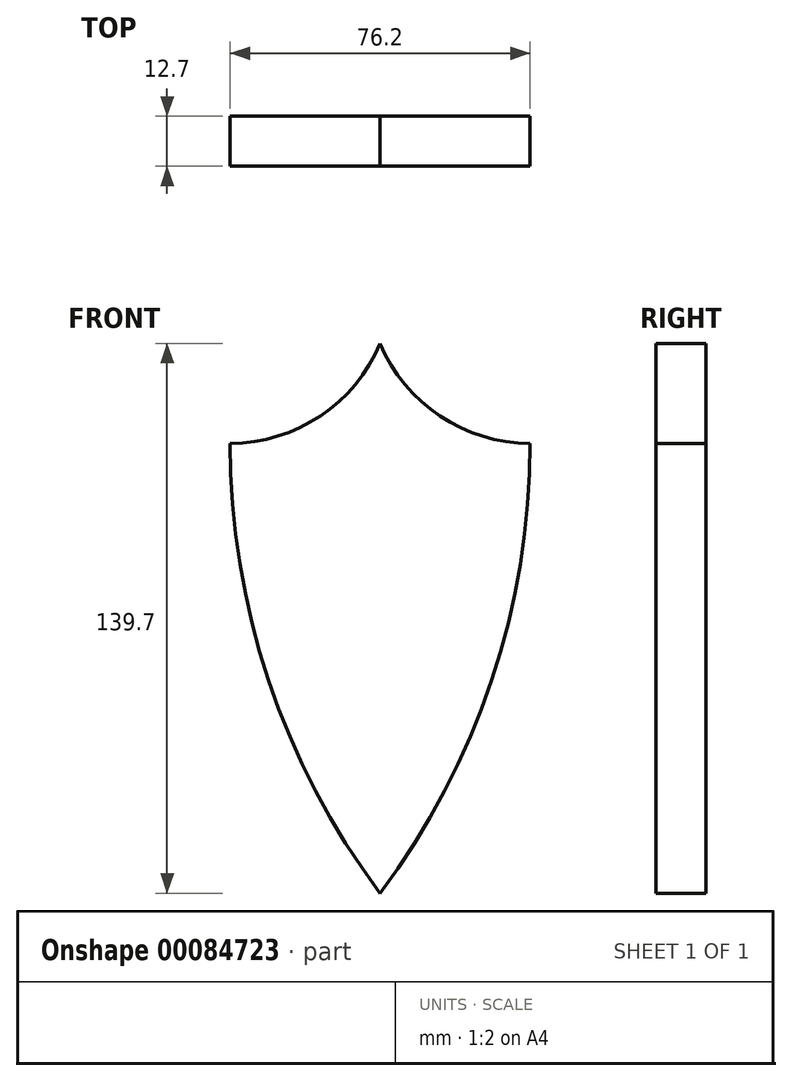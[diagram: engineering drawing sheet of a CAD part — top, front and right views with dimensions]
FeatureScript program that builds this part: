
annotation { "Feature Type Name" : "Feature", "Feature Type Description" : "" }
export const myFeature = defineFeature(function(context is Context, id is Id, definition is map)
    precondition{}
    {
        {
            var Q0;
            Q0=qCreatedBy(makeId("Front.planeOp"),FACE);
            var sketch = newSketch(context, id + "F0", { "sketchPlane" : qUnion([Q0])});
            skLineSegment(sketch, "E0", {"start": v(0, -38.1) * mm, "end": v(0, 0) * mm});
            skLineSegment(sketch, "E1", {"start": v(0, 0) * mm, "end": v(-38.1, 0) * mm});
            skLineSegment(sketch, "E2", {"start": v(0, 0) * mm, "end": v(0, 25.4) * mm});
            skLineSegment(sketch, "E3", {"start": v(0, -38.1) * mm, "end": v(0, -114.3) * mm});
            skArc(sketch, "E4", {"start": v(-38.1, 0) * mm, "mid": v(-28.32, -60.24) * mm, "end": v(0, -114.3) * mm});
            skArc(sketch, "E5", {"start": v(-38.1, 0) * mm, "mid": v(-15.2, 6.93) * mm, "end": v(0, 25.4) * mm});
            skArc(sketch, "E6.MirrorCS", {"start": v(38.1, 0) * mm, "mid": v(28.32, -60.24) * mm, "end": v(0, -114.3) * mm});
            skLineSegment(sketch, "E7.MirrorCS", {"start": v(0, 0) * mm, "end": v(38.1, 0) * mm});
            skArc(sketch, "E8.MirrorCS", {"start": v(38.1, 0) * mm, "mid": v(15.2, 6.93) * mm, "end": v(0, 25.4) * mm});
            skSolve(sketch);
        }
        {
            var Q0;
            Q0=makeQuery(id+"F0.imprint","IMPRINT",FACE,{"disambiguationData":[TD([[makeQuery(id+"F0.imprint","IMPRINT",EDGE,{"derivedFrom":sQuery(id+"F0.wireOp",EDGE,"E0")}),1.0]])]});
            var Q1;
            Q1=makeQuery(id+"F0.imprint","IMPRINT",FACE,{"disambiguationData":[TD([[makeQuery(id+"F0.imprint","IMPRINT",EDGE,{"derivedFrom":sQuery(id+"F0.wireOp",EDGE,"E0")}),-1.0]])]});
            var Q2;
            Q2=makeQuery(id+"F0.imprint","IMPRINT",FACE,{"disambiguationData":[TD([[makeQuery(id+"F0.imprint","IMPRINT",EDGE,{"derivedFrom":sQuery(id+"F0.wireOp",EDGE,"E2")}),-1.0]])]});
            var Q3;
            Q3=makeQuery(id+"F0.imprint","IMPRINT",FACE,{"disambiguationData":[TD([[makeQuery(id+"F0.imprint","IMPRINT",EDGE,{"derivedFrom":sQuery(id+"F0.wireOp",EDGE,"E1")}),-1.0]])]});
            extrude(context, id + "F1", {"entities" : qUnion([Q0, Q1, Q2, Q3]), "depth" : 12.7 * mm, "offsetDistance" : 25.4 * mm});
        }
    });
